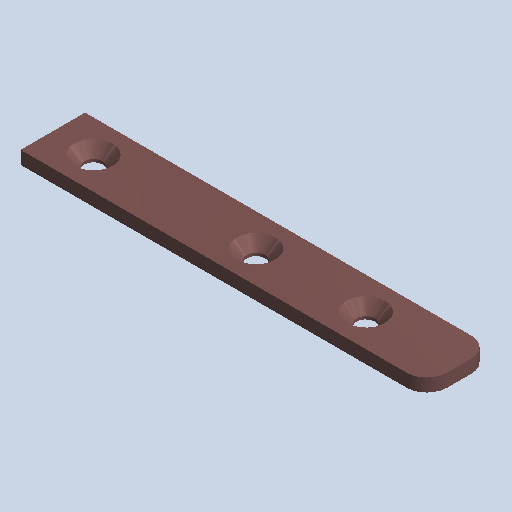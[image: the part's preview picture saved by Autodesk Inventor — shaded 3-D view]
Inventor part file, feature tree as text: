
AUTODESK INVENTOR PART (.ipt)
format: ipt  version: 2022.1 (Build 261234000, 234)  size: 73,728 bytes
history: native  units: mm (DEFAULTED — no unit token found)
features: other x8, fillet x1
bodies: Body1 (feature_tree)
feature tree (9):
  other  "Sólido1"
  other  "Origen"
  other  "Plano YZ"
  other  "Plano XZ"
  other  "Plano XY"
  other  "Eje X"
  other  "Eje Y"
  other  "Eje Z"
  fillet  "Fillet1"  [1 undecoded]
note: 1 required parameter value undecoded (feature->parameter linkage not recoverable at this tier; creation-order binding heuristic only, values carry confidence <= 0.55)
